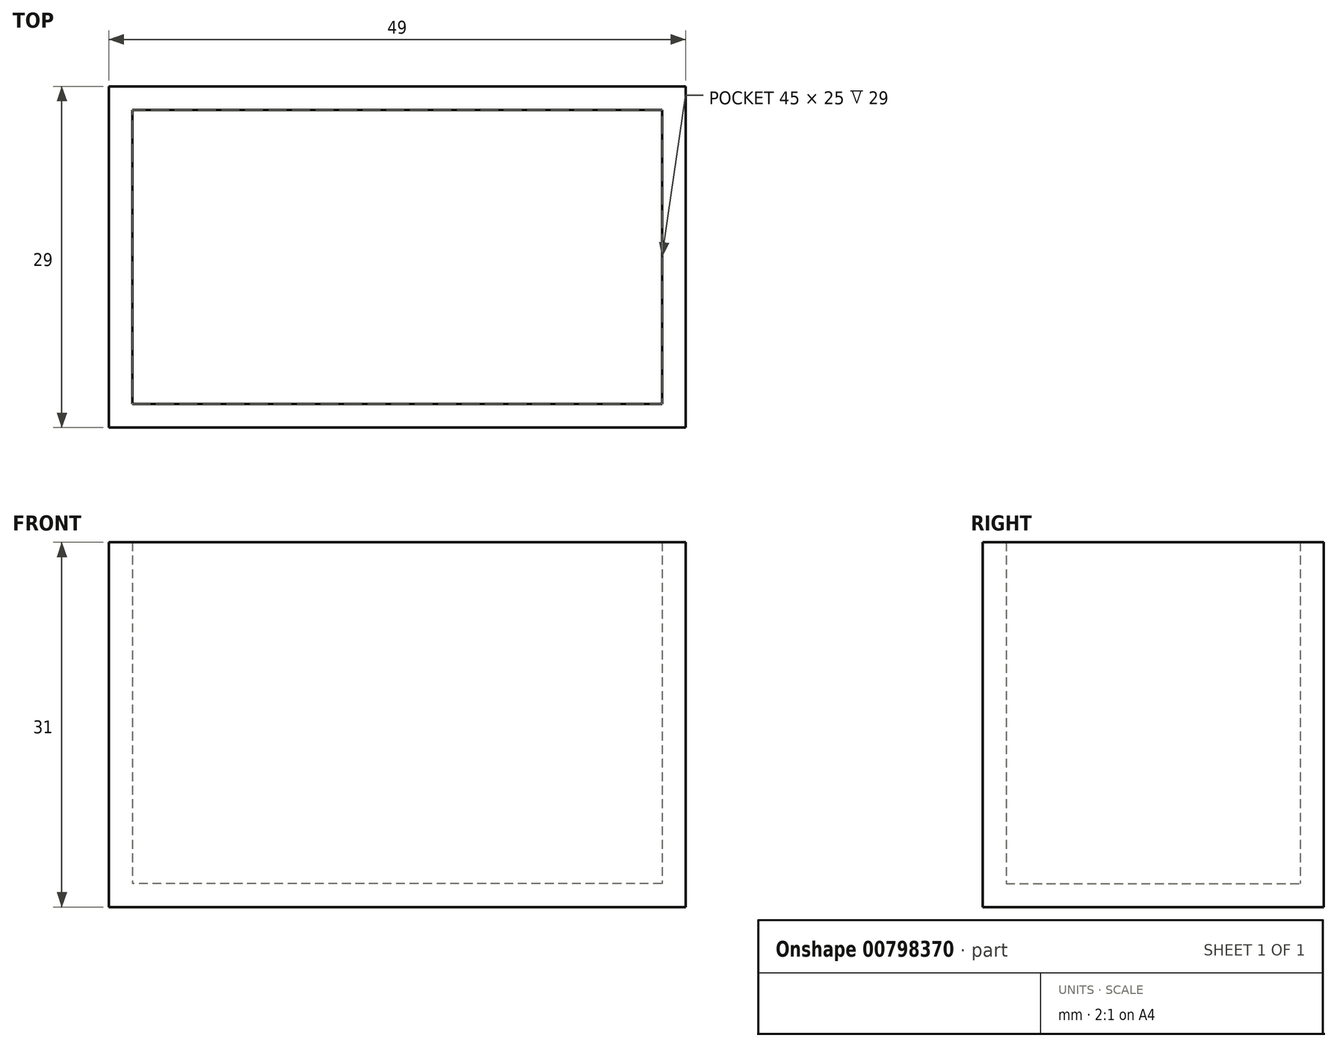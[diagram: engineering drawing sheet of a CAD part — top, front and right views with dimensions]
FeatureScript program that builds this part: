
annotation { "Feature Type Name" : "Feature", "Feature Type Description" : "" }
export const myFeature = defineFeature(function(context is Context, id is Id, definition is map)
    precondition{}
    {
        {
            var Q0;
            Q0=qCreatedBy(makeId("Top.planeOp"),FACE);
            var sketch = newSketch(context, id + "F0", { "sketchPlane" : qUnion([Q0])});
            skPoint(sketch, "E0.middle", {"position": v(0, 0) * mm});
            skLineSegment(sketch, "E1.bottom", {"start": v(24.5, -14.5) * mm, "end": v(-24.5, -14.5) * mm});
            skLineSegment(sketch, "E1.top", {"start": v(24.5, 14.5) * mm, "end": v(-24.5, 14.5) * mm});
            skLineSegment(sketch, "E1.left", {"start": v(24.5, -14.5) * mm, "end": v(24.5, 14.5) * mm});
            skLineSegment(sketch, "E1.right", {"start": v(-24.5, -14.5) * mm, "end": v(-24.5, 14.5) * mm});
            skSolve(sketch);
        }
        {
            var Q0;
            Q0=makeQuery(id+"F0.imprint","IMPRINT",FACE,{"disambiguationData":[TD([[makeQuery(id+"F0.imprint","IMPRINT",EDGE,{"derivedFrom":sQuery(id+"F0.wireOp",EDGE,"E1.bottom")}),-1.0]])]});
            extrude(context, id + "F1", {"entities" : qUnion([Q0]), "depth" : 31 * mm, "offsetDistance" : 25 * mm});
        }
        {
            var Q0;
            Q0=makeQuery(id+"F1.opExtrude","CAP_FACE",FACE,{"disambiguationData":[OSD([sQuery(id+"F0.wireOp",EDGE,"E1.bottom"),sQuery(id+"F0.wireOp",EDGE,"E1.top"),sQuery(id+"F0.wireOp",EDGE,"E1.left"),sQuery(id+"F0.wireOp",EDGE,"E1.right")])],"isStart":false});
            shell(context, id + "F2", {"entities" : qUnion([Q0]), "thickness" : 2 * mm});
        }
    });
